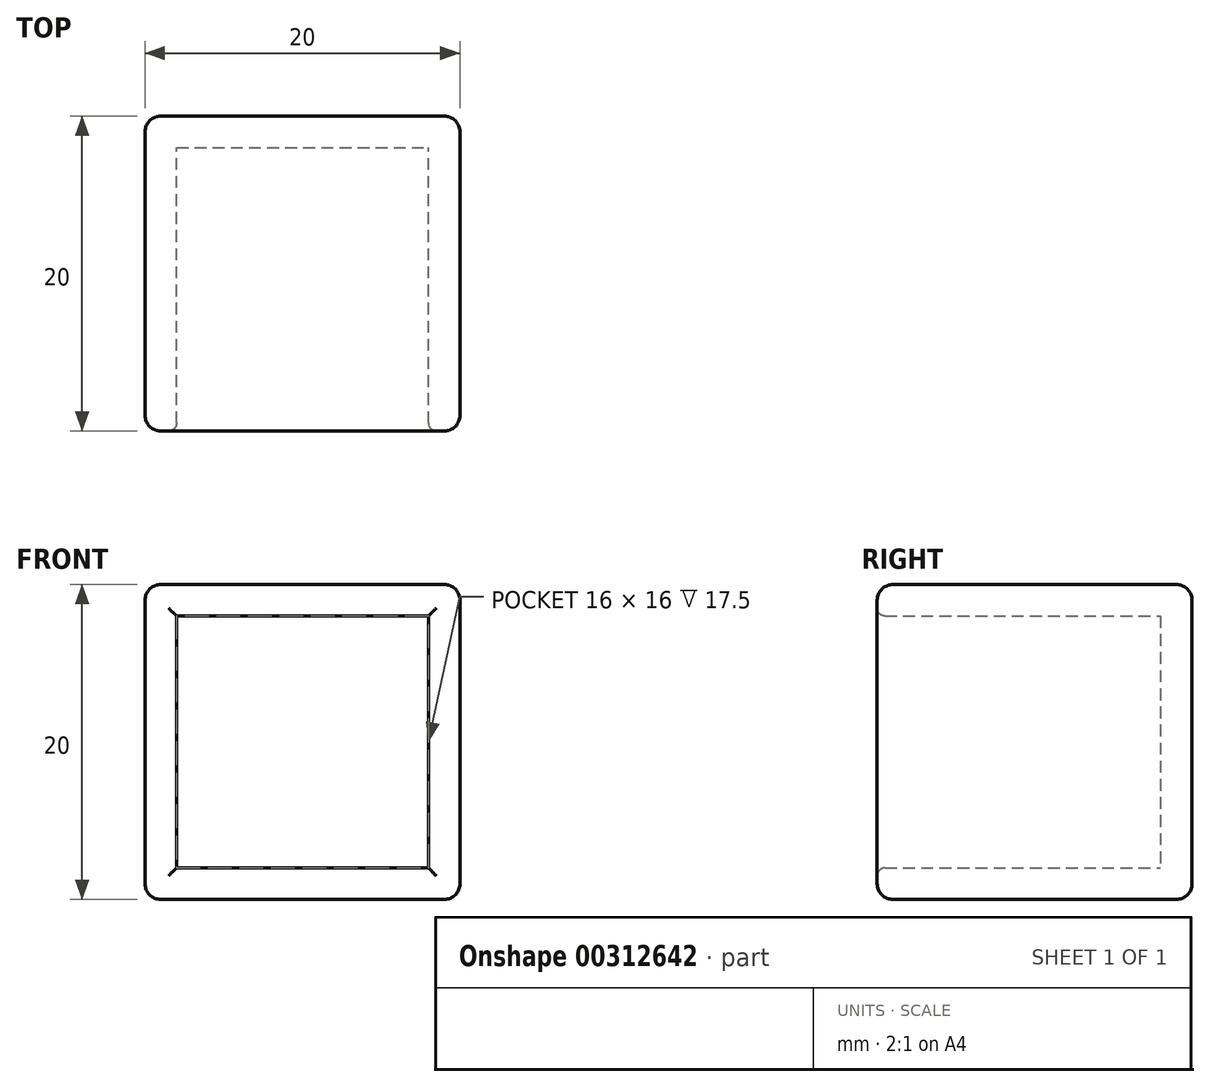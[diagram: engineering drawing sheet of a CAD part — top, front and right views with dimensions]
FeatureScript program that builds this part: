
annotation { "Feature Type Name" : "Feature", "Feature Type Description" : "" }
export const myFeature = defineFeature(function(context is Context, id is Id, definition is map)
    precondition{}
    {
        {
            var Q0;
            Q0=qCreatedBy(makeId("Front.planeOp"),FACE);
            var sketch = newSketch(context, id + "F0", { "sketchPlane" : qUnion([Q0])});
            skLineSegment(sketch, "E0.bottom", {"start": v(-10, 10) * mm, "end": v(10, 10) * mm});
            skLineSegment(sketch, "E0.top", {"start": v(-10, -10) * mm, "end": v(10, -10) * mm});
            skLineSegment(sketch, "E0.left", {"start": v(-10, 10) * mm, "end": v(-10, -10) * mm});
            skLineSegment(sketch, "E0.right", {"start": v(10, 10) * mm, "end": v(10, -10) * mm});
            skPoint(sketch, "E0.middle", {"position": v(0, 0) * mm});
            skSolve(sketch);
        }
        {
            var Q0;
            Q0=makeQuery(id+"F0.imprint","IMPRINT",FACE,{"disambiguationData":[TD([[makeQuery(id+"F0.imprint","IMPRINT",EDGE,{"derivedFrom":sQuery(id+"F0.wireOp",EDGE,"E0.bottom")}),-1.0]])]});
            extrude(context, id + "F1", {"entities" : qUnion([Q0]), "endBound" : BoundingType.SYMMETRIC, "depth" : 20 * mm});
        }
        {
            var Q0;
            Q0=makeQuery(id+"F1.opExtrude","CAP_FACE",FACE,{"disambiguationData":[OSD([sQuery(id+"F0.wireOp",EDGE,"E0.bottom"),sQuery(id+"F0.wireOp",EDGE,"E0.top"),sQuery(id+"F0.wireOp",EDGE,"E0.left"),sQuery(id+"F0.wireOp",EDGE,"E0.right")])],"isStart":false});
            shell(context, id + "F2", {"entities" : qUnion([Q0]), "thickness" : 2 * mm});
        }
        {
            var Q0;
            Q0=makeQuery(id+"F1.opExtrude","CAP_EDGE",EDGE,{"disambiguationData":[OSD([sQuery(id+"F0.wireOp",EDGE,"E0.top")])],"isStart":false});
            var Q1;
            Q1=makeQuery(id+"F1.opExtrude","SWEPT_FACE",FACE,{"disambiguationData":[OSD([sQuery(id+"F0.wireOp",EDGE,"E0.right")])]});
            var Q2;
            Q2=makeQuery(id+"F1.opExtrude","SWEPT_FACE",FACE,{"disambiguationData":[OSD([sQuery(id+"F0.wireOp",EDGE,"E0.top")])]});
            var Q3;
            Q3=makeQuery(id+"F1.opExtrude","CAP_EDGE",EDGE,{"disambiguationData":[OSD([sQuery(id+"F0.wireOp",EDGE,"E0.left")])],"isStart":false});
            var Q4;
            Q4=makeQuery(id+"F1.opExtrude","SWEPT_EDGE",EDGE,{"disambiguationData":[OSD([sQuery(id+"F0.wireOp",EDGE,"E0.bottom"),sQuery(id+"F0.wireOp",EDGE,"E0.left")])]});
            var Q5;
            Q5=makeQuery(id+"F1.opExtrude","CAP_EDGE",EDGE,{"disambiguationData":[OSD([sQuery(id+"F0.wireOp",EDGE,"E0.left")])],"isStart":true});
            var Q6;
            Q6=makeQuery(id+"F1.opExtrude","CAP_EDGE",EDGE,{"disambiguationData":[OSD([sQuery(id+"F0.wireOp",EDGE,"E0.bottom")])],"isStart":true});
            var Q7;
            Q7=makeQuery(id+"F1.opExtrude","CAP_EDGE",EDGE,{"disambiguationData":[OSD([sQuery(id+"F0.wireOp",EDGE,"E0.bottom")])],"isStart":false});
            fillet(context, id + "F3", {"entities" : qUnion([Q0, Q1, Q2, Q3, Q4, Q5, Q6, Q7]), "radius" : 1 * mm, "tangentPropagation" : true, "allowEdgeOverflow" : false});
        }
        {
            var Q0;
            {var subQ0=sQuery(id+"F0.wireOp",EDGE,"E0.left");Q0=makeQuery(id+"F2.opShell","OFFSET_EDGE",EDGE,{"disambiguationData":[OSD([subQ0]),TDD([makeQuery(id+"F1.opExtrude","CAP_EDGE",EDGE,{"disambiguationData":[OSD([subQ0])],"isStart":false})])]});}
            var Q1;
            {var subQ0=sQuery(id+"F0.wireOp",EDGE,"E0.top");Q1=makeQuery(id+"F2.opShell","OFFSET_EDGE",EDGE,{"disambiguationData":[OSD([subQ0]),TDD([makeQuery(id+"F1.opExtrude","CAP_EDGE",EDGE,{"disambiguationData":[OSD([subQ0])],"isStart":false})])]});}
            var Q2;
            {var subQ0=sQuery(id+"F0.wireOp",EDGE,"E0.right");Q2=makeQuery(id+"F2.opShell","OFFSET_EDGE",EDGE,{"disambiguationData":[OSD([subQ0]),TDD([makeQuery(id+"F1.opExtrude","CAP_EDGE",EDGE,{"disambiguationData":[OSD([subQ0])],"isStart":false})])]});}
            var Q3;
            Q3=makeQuery(id+"F1.opExtrude","CAP_FACE",FACE,{"disambiguationData":[OSD([sQuery(id+"F0.wireOp",EDGE,"E0.bottom"),sQuery(id+"F0.wireOp",EDGE,"E0.top"),sQuery(id+"F0.wireOp",EDGE,"E0.left"),sQuery(id+"F0.wireOp",EDGE,"E0.right")])],"isStart":false});
            fillet(context, id + "F4", {"entities" : qUnion([Q0, Q1, Q2, Q3]), "radius" : 0.5 * mm, "tangentPropagation" : true, "allowEdgeOverflow" : false});
        }
    });
